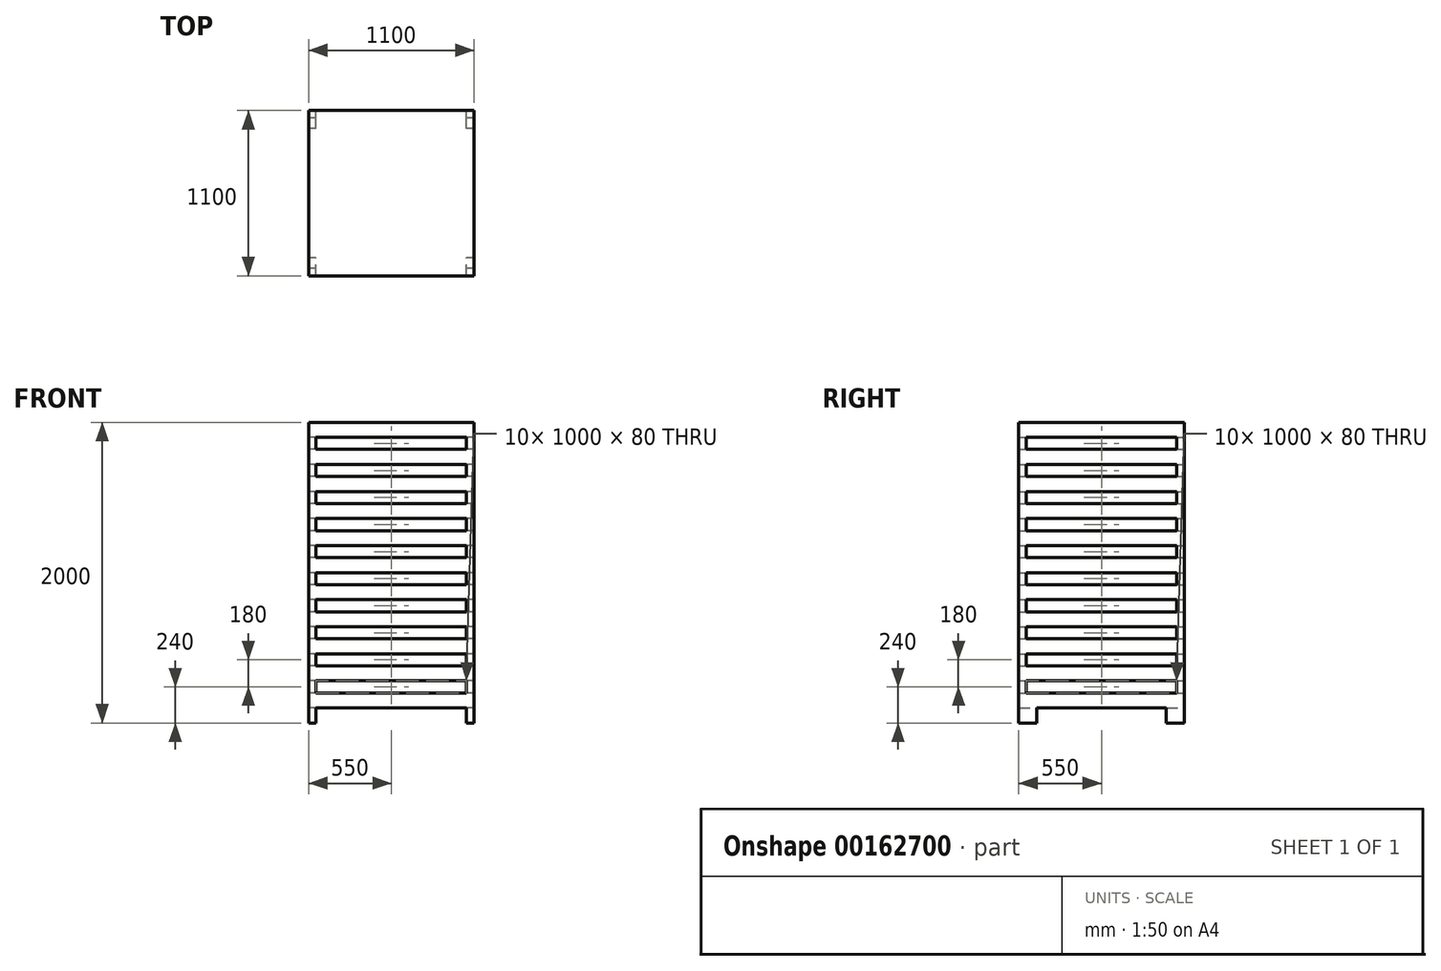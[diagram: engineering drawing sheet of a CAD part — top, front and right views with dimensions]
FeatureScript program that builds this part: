
annotation { "Feature Type Name" : "Feature", "Feature Type Description" : "" }
export const myFeature = defineFeature(function(context is Context, id is Id, definition is map)
    precondition{}
    {
        {
            var Q0;
            Q0=qCreatedBy(makeId("Front.planeOp"),FACE);
            var sketch = newSketch(context, id + "F0", { "sketchPlane" : qUnion([Q0])});
            skLineSegment(sketch, "E0", {"start": v(0, 0) * mm, "end": v(0, 2000) * mm});
            skLineSegment(sketch, "E1", {"start": v(0, 2000) * mm, "end": v(1100, 2000) * mm});
            skLineSegment(sketch, "E2", {"start": v(1100, 2000) * mm, "end": v(1100, 0) * mm});
            skLineSegment(sketch, "E3", {"start": v(1100, 0) * mm, "end": v(1050, 0) * mm});
            skLineSegment(sketch, "E4", {"start": v(1050, 0) * mm, "end": v(1050, 100) * mm});
            skLineSegment(sketch, "E5", {"start": v(1050, 100) * mm, "end": v(50, 100) * mm});
            skLineSegment(sketch, "E6", {"start": v(50, 100) * mm, "end": v(50, 0) * mm});
            skLineSegment(sketch, "E7", {"start": v(50, 0) * mm, "end": v(0, 0) * mm});
            skLineSegment(sketch, "E8.bottom", {"start": v(50, 1900) * mm, "end": v(1050, 1900) * mm});
            skLineSegment(sketch, "E8.top", {"start": v(50, 1820) * mm, "end": v(1050, 1820) * mm});
            skLineSegment(sketch, "E8.left", {"start": v(50, 1900) * mm, "end": v(50, 1820) * mm});
            skLineSegment(sketch, "E8.right", {"start": v(1050, 1900) * mm, "end": v(1050, 1820) * mm});
            skLineSegment(sketch, "E9.bottom", {"start": v(50, 1720) * mm, "end": v(1050, 1720) * mm});
            skLineSegment(sketch, "E9.top", {"start": v(50, 1640) * mm, "end": v(1050, 1640) * mm});
            skLineSegment(sketch, "E9.left", {"start": v(50, 1720) * mm, "end": v(50, 1640) * mm});
            skLineSegment(sketch, "E9.right", {"start": v(1050, 1720) * mm, "end": v(1050, 1640) * mm});
            skLineSegment(sketch, "E10.bottom", {"start": v(50, 1540) * mm, "end": v(1050, 1540) * mm});
            skLineSegment(sketch, "E10.top", {"start": v(50, 1460) * mm, "end": v(1050, 1460) * mm});
            skLineSegment(sketch, "E10.left", {"start": v(50, 1540) * mm, "end": v(50, 1460) * mm});
            skLineSegment(sketch, "E10.right", {"start": v(1050, 1540) * mm, "end": v(1050, 1460) * mm});
            skLineSegment(sketch, "E11.bottom", {"start": v(50, 1180) * mm, "end": v(1050, 1180) * mm});
            skLineSegment(sketch, "E11.top", {"start": v(50, 1100) * mm, "end": v(1050, 1100) * mm});
            skLineSegment(sketch, "E11.left", {"start": v(50, 1180) * mm, "end": v(50, 1100) * mm});
            skLineSegment(sketch, "E11.right", {"start": v(1050, 1180) * mm, "end": v(1050, 1100) * mm});
            skLineSegment(sketch, "E12.bottom", {"start": v(50, 820) * mm, "end": v(1050, 820) * mm});
            skLineSegment(sketch, "E12.top", {"start": v(50, 740) * mm, "end": v(1050, 740) * mm});
            skLineSegment(sketch, "E12.left", {"start": v(50, 820) * mm, "end": v(50, 740) * mm});
            skLineSegment(sketch, "E12.right", {"start": v(1050, 820) * mm, "end": v(1050, 740) * mm});
            skLineSegment(sketch, "E13.bottom", {"start": v(50, 640) * mm, "end": v(1050, 640) * mm});
            skLineSegment(sketch, "E13.top", {"start": v(50, 560) * mm, "end": v(1050, 560) * mm});
            skLineSegment(sketch, "E13.left", {"start": v(50, 640) * mm, "end": v(50, 560) * mm});
            skLineSegment(sketch, "E13.right", {"start": v(1050, 640) * mm, "end": v(1050, 560) * mm});
            skLineSegment(sketch, "E14.bottom", {"start": v(50, 460) * mm, "end": v(1050, 460) * mm});
            skLineSegment(sketch, "E14.top", {"start": v(50, 380) * mm, "end": v(1050, 380) * mm});
            skLineSegment(sketch, "E14.left", {"start": v(50, 460) * mm, "end": v(50, 380) * mm});
            skLineSegment(sketch, "E14.right", {"start": v(1050, 460) * mm, "end": v(1050, 380) * mm});
            skLineSegment(sketch, "E15.bottom", {"start": v(50, 1360) * mm, "end": v(1050, 1360) * mm});
            skLineSegment(sketch, "E15.top", {"start": v(50, 1280) * mm, "end": v(1050, 1280) * mm});
            skLineSegment(sketch, "E15.left", {"start": v(50, 1360) * mm, "end": v(50, 1280) * mm});
            skLineSegment(sketch, "E15.right", {"start": v(1050, 1360) * mm, "end": v(1050, 1280) * mm});
            skLineSegment(sketch, "E16.bottom", {"start": v(1050, 1000) * mm, "end": v(50, 1000) * mm});
            skLineSegment(sketch, "E16.top", {"start": v(1050, 920) * mm, "end": v(50, 920) * mm});
            skLineSegment(sketch, "E16.left", {"start": v(1050, 1000) * mm, "end": v(1050, 920) * mm});
            skLineSegment(sketch, "E16.right", {"start": v(50, 1000) * mm, "end": v(50, 920) * mm});
            skLineSegment(sketch, "E17.bottom", {"start": v(50, 280) * mm, "end": v(1050, 280) * mm});
            skLineSegment(sketch, "E17.top", {"start": v(50, 200) * mm, "end": v(1050, 200) * mm});
            skLineSegment(sketch, "E17.left", {"start": v(50, 280) * mm, "end": v(50, 200) * mm});
            skLineSegment(sketch, "E17.right", {"start": v(1050, 280) * mm, "end": v(1050, 200) * mm});
            skSolve(sketch);
        }
        {
            var Q0;
            Q0 = qSketchRegion(id + "F0", true);
            extrude(context, id + "F1", {"entities" : qUnion([Q0]), "depth" : 1100 * mm});
        }
        {
            var Q0;
            Q0=makeQuery(id+"F1.opExtrude","SWEPT_FACE",FACE,{"disambiguationData":[OSD([sQuery(id+"F0.wireOp",EDGE,"E0")])]});
            var sketch = newSketch(context, id + "F2", { "sketchPlane" : qUnion([Q0])});
            skLineSegment(sketch, "E18.bottom", {"start": v(1050, 1900) * mm, "end": v(50, 1900) * mm});
            skLineSegment(sketch, "E18.top", {"start": v(1050, 1820) * mm, "end": v(50, 1820) * mm});
            skLineSegment(sketch, "E18.left", {"start": v(1050, 1900) * mm, "end": v(1050, 1820) * mm});
            skLineSegment(sketch, "E18.right", {"start": v(50, 1900) * mm, "end": v(50, 1820) * mm});
            skLineSegment(sketch, "E19.bottom", {"start": v(1050, 1720) * mm, "end": v(50, 1720) * mm});
            skLineSegment(sketch, "E19.top", {"start": v(1050, 1640) * mm, "end": v(50, 1640) * mm});
            skLineSegment(sketch, "E19.left", {"start": v(1050, 1720) * mm, "end": v(1050, 1640) * mm});
            skLineSegment(sketch, "E19.right", {"start": v(50, 1720) * mm, "end": v(50, 1640) * mm});
            skLineSegment(sketch, "E20.bottom", {"start": v(1050, 1540) * mm, "end": v(50, 1540) * mm});
            skLineSegment(sketch, "E20.top", {"start": v(1050, 1460) * mm, "end": v(50, 1460) * mm});
            skLineSegment(sketch, "E20.left", {"start": v(1050, 1540) * mm, "end": v(1050, 1460) * mm});
            skLineSegment(sketch, "E20.right", {"start": v(50, 1540) * mm, "end": v(50, 1460) * mm});
            skLineSegment(sketch, "E21.bottom", {"start": v(1050, 1360) * mm, "end": v(50, 1360) * mm});
            skLineSegment(sketch, "E21.top", {"start": v(1050, 1280) * mm, "end": v(50, 1280) * mm});
            skLineSegment(sketch, "E21.left", {"start": v(1050, 1360) * mm, "end": v(1050, 1280) * mm});
            skLineSegment(sketch, "E21.right", {"start": v(50, 1360) * mm, "end": v(50, 1280) * mm});
            skLineSegment(sketch, "E22.bottom", {"start": v(1050, 1180) * mm, "end": v(50, 1180) * mm});
            skLineSegment(sketch, "E22.top", {"start": v(1050, 1100) * mm, "end": v(50, 1100) * mm});
            skLineSegment(sketch, "E22.left", {"start": v(1050, 1180) * mm, "end": v(1050, 1100) * mm});
            skLineSegment(sketch, "E22.right", {"start": v(50, 1180) * mm, "end": v(50, 1100) * mm});
            skLineSegment(sketch, "E23.bottom", {"start": v(1050, 1000) * mm, "end": v(50, 1000) * mm});
            skLineSegment(sketch, "E23.top", {"start": v(1050, 920) * mm, "end": v(50, 920) * mm});
            skLineSegment(sketch, "E23.left", {"start": v(1050, 1000) * mm, "end": v(1050, 920) * mm});
            skLineSegment(sketch, "E23.right", {"start": v(50, 1000) * mm, "end": v(50, 920) * mm});
            skLineSegment(sketch, "E24.bottom", {"start": v(1050, 820) * mm, "end": v(50, 820) * mm});
            skLineSegment(sketch, "E24.top", {"start": v(1050, 740) * mm, "end": v(50, 740) * mm});
            skLineSegment(sketch, "E24.left", {"start": v(1050, 820) * mm, "end": v(1050, 740) * mm});
            skLineSegment(sketch, "E24.right", {"start": v(50, 820) * mm, "end": v(50, 740) * mm});
            skLineSegment(sketch, "E25.bottom", {"start": v(1050, 640) * mm, "end": v(50, 640) * mm});
            skLineSegment(sketch, "E25.top", {"start": v(1050, 560) * mm, "end": v(50, 560) * mm});
            skLineSegment(sketch, "E25.left", {"start": v(1050, 640) * mm, "end": v(1050, 560) * mm});
            skLineSegment(sketch, "E25.right", {"start": v(50, 640) * mm, "end": v(50, 560) * mm});
            skLineSegment(sketch, "E26.bottom", {"start": v(1050, 460) * mm, "end": v(50, 460) * mm});
            skLineSegment(sketch, "E26.top", {"start": v(1050, 380) * mm, "end": v(50, 380) * mm});
            skLineSegment(sketch, "E26.left", {"start": v(1050, 460) * mm, "end": v(1050, 380) * mm});
            skLineSegment(sketch, "E26.right", {"start": v(50, 460) * mm, "end": v(50, 380) * mm});
            skLineSegment(sketch, "E27.bottom", {"start": v(1050, 200) * mm, "end": v(50, 200) * mm});
            skLineSegment(sketch, "E27.top", {"start": v(1050, 280) * mm, "end": v(50, 280) * mm});
            skLineSegment(sketch, "E27.left", {"start": v(1050, 280) * mm, "end": v(1050, 200) * mm});
            skLineSegment(sketch, "E27.right", {"start": v(50, 280) * mm, "end": v(50, 200) * mm});
            skLineSegment(sketch, "E28.bottom", {"start": v(980, 0) * mm, "end": v(120, 0) * mm});
            skLineSegment(sketch, "E28.top", {"start": v(980, 100) * mm, "end": v(120, 100) * mm});
            skLineSegment(sketch, "E28.left", {"start": v(980, 0) * mm, "end": v(980, 100) * mm});
            skLineSegment(sketch, "E28.right", {"start": v(120, 0) * mm, "end": v(120, 100) * mm});
            skSolve(sketch);
        }
        {
            var Q0;
            Q0 = qSketchRegion(id + "F2", true);
            extrude(context, id + "F3", {"entities" : qUnion([Q0]), "operationType" : NewBodyOperationType.REMOVE, "endBound" : BoundingType.THROUGH_ALL, "oppositeDirection" : true, "depth" : 25 * mm});
        }
    });
